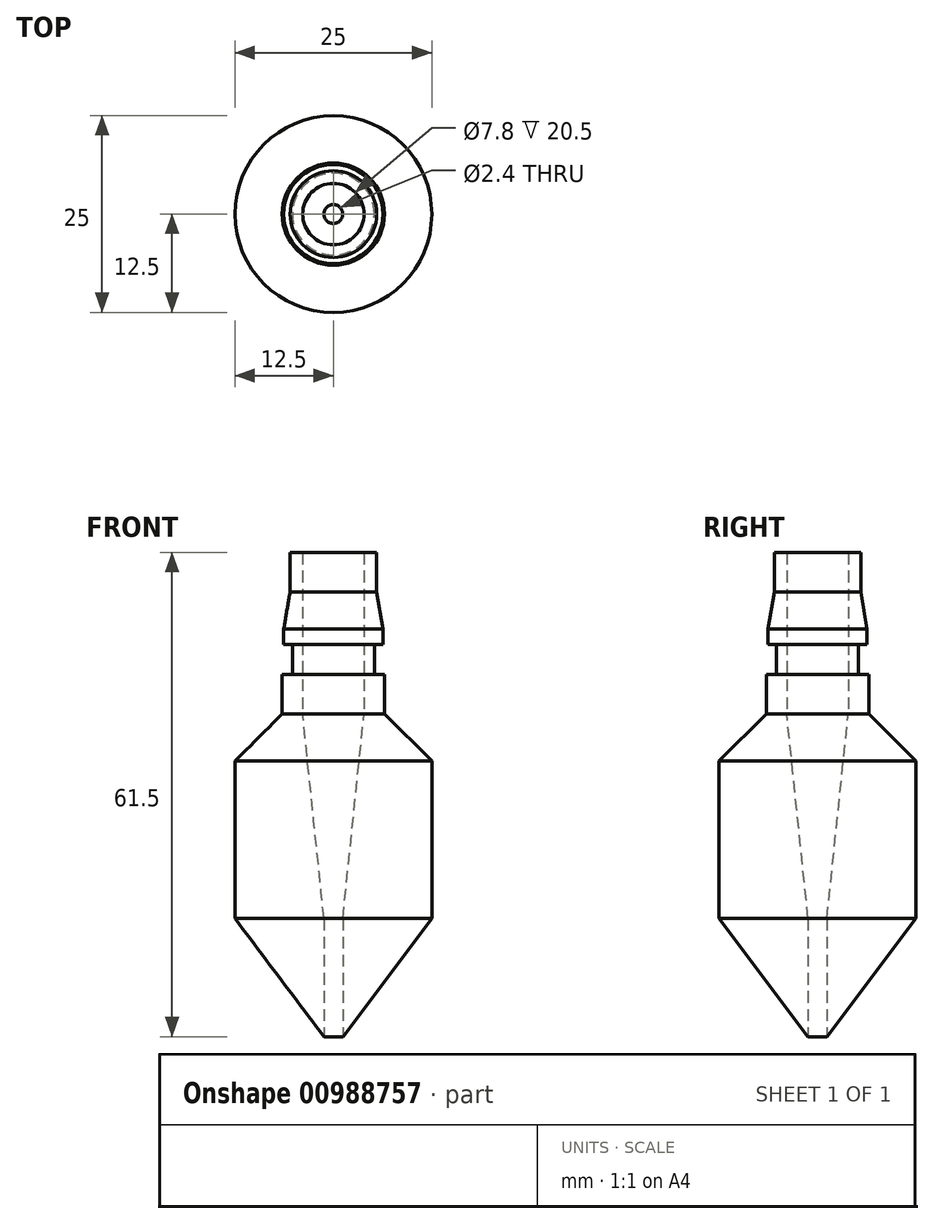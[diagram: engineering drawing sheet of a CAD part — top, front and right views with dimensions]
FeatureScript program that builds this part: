
annotation { "Feature Type Name" : "Feature", "Feature Type Description" : "" }
export const myFeature = defineFeature(function(context is Context, id is Id, definition is map)
    precondition{}
    {
        {
            var Q0;
            Q0=qCreatedBy(makeId("Front.planeOp"),FACE);
            var sketch = newSketch(context, id + "F0", { "sketchPlane" : qUnion([Q0])});
            skLineSegment(sketch, "E0", {"start": v(0, 0) * mm, "end": v(0, 20.5) * mm});
            skLineSegment(sketch, "E1", {"start": v(3.9, 20.5) * mm, "end": v(5.5, 20.5) * mm});
            skLineSegment(sketch, "E2", {"start": v(5.5, 20.5) * mm, "end": v(5.5, 15.5) * mm});
            skLineSegment(sketch, "E3", {"start": v(6.3, 10.8) * mm, "end": v(5.5, 15.5) * mm});
            skLineSegment(sketch, "E4", {"start": v(6.3, 10.8) * mm, "end": v(6.3, 8.8) * mm});
            skLineSegment(sketch, "E5", {"start": v(5.2, 5) * mm, "end": v(5.2, 8.8) * mm});
            skLineSegment(sketch, "E6", {"start": v(5.2, 8.8) * mm, "end": v(6.3, 8.8) * mm});
            skLineSegment(sketch, "E7", {"start": v(5.2, 5) * mm, "end": v(6.5, 5) * mm});
            skLineSegment(sketch, "E8", {"start": v(6.5, 5) * mm, "end": v(6.5, 0) * mm});
            skLineSegment(sketch, "E9", {"start": v(3.9, 20.5) * mm, "end": v(3.9, 0) * mm});
            skLineSegment(sketch, "E10", {"start": v(12.5, -6) * mm, "end": v(6.5, 0) * mm});
            skLineSegment(sketch, "E11", {"start": v(12.5, -6) * mm, "end": v(12.5, -26) * mm});
            skLineSegment(sketch, "E12", {"start": v(1.2, -41) * mm, "end": v(1.2, -26) * mm});
            skLineSegment(sketch, "E13", {"start": v(1.2, -41) * mm, "end": v(12.5, -26) * mm});
            skLineSegment(sketch, "E14", {"start": v(3.9, 0) * mm, "end": v(1.2, -26) * mm});
            skSolve(sketch);
        }
        {
            var Q0;
            Q0=makeQuery(id+"F0.imprint","IMPRINT",FACE,{"disambiguationData":[TD([[makeQuery(id+"F0.imprint","IMPRINT",EDGE,{"derivedFrom":sQuery(id+"F0.wireOp",EDGE,"E1")}),-1.0]])]});
            var Q1;
            Q1=sQuery(id+"F0.wireOp",EDGE,"E0");
            revolve(context, id + "F1", {"surfaceOperationType" : NewSurfaceOperationType.NEW, "entities" : qUnion([Q0]), "axis" : qUnion([Q1]), "revolveType" : RevolveType.FULL});
        }
    });
